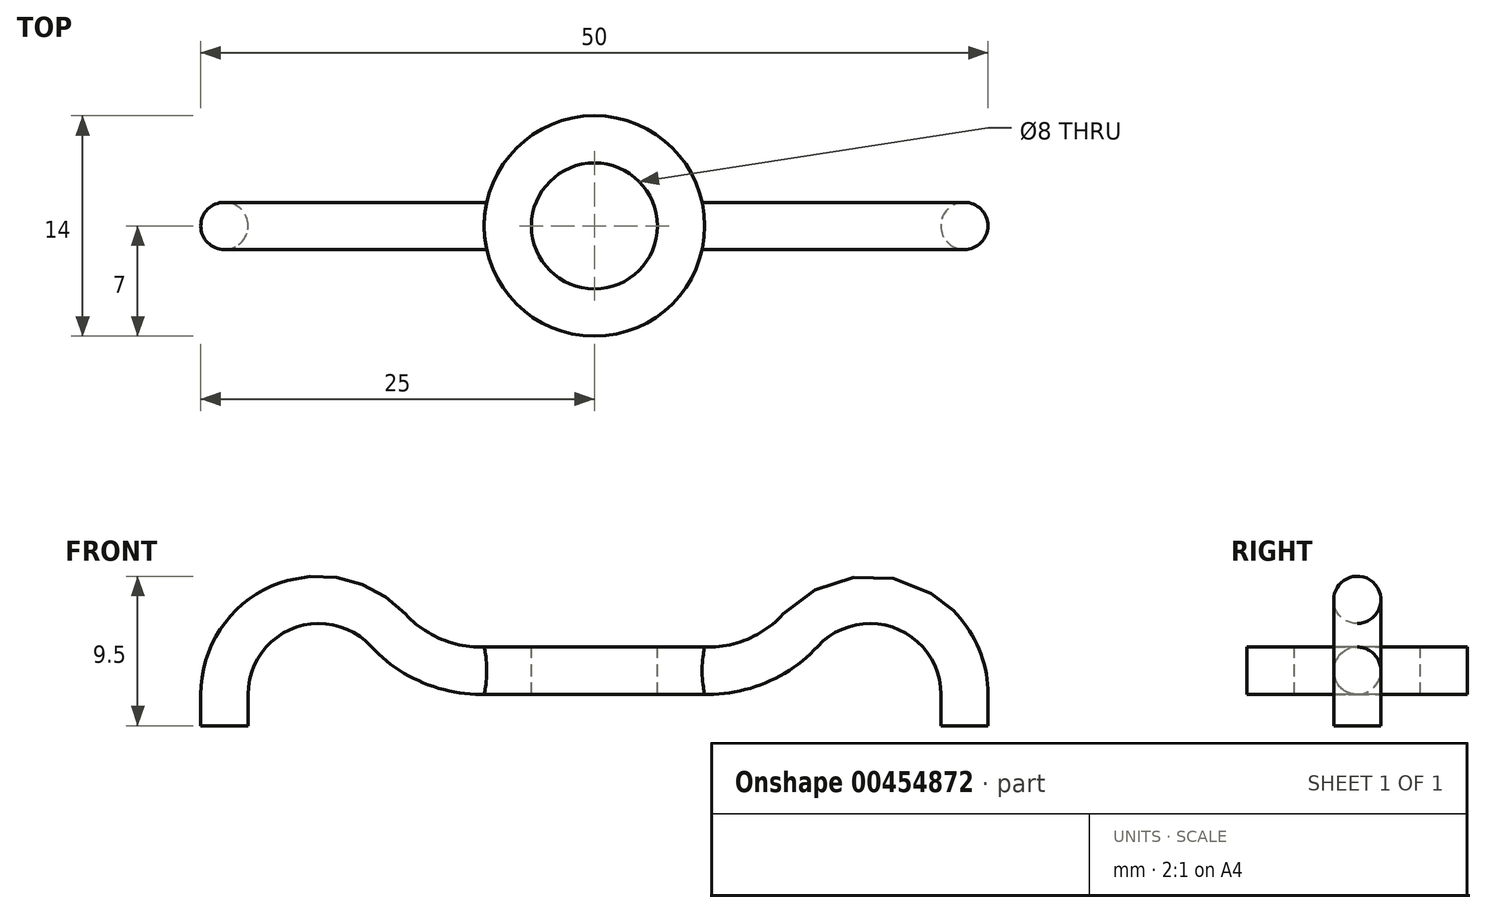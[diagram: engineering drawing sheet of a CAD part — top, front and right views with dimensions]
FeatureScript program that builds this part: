
annotation { "Feature Type Name" : "Feature", "Feature Type Description" : "" }
export const myFeature = defineFeature(function(context is Context, id is Id, definition is map)
    precondition{}
    {
        {
            var Q0;
            Q0=qCreatedBy(makeId("Front.planeOp"),FACE);
            var sketch = newSketch(context, id + "F0", { "sketchPlane" : qUnion([Q0])});
            skLineSegment(sketch, "E0", {"start": v(-25, 0) * mm, "end": v(-25, -2) * mm});
            skLineSegment(sketch, "E1", {"start": v(-7.22, 3) * mm, "end": v(0, 3) * mm});
            skArc(sketch, "E2", {"start": v(-25, 0) * mm, "mid": v(-20.23, 6.98) * mm, "end": v(-12, 5.09) * mm});
            skArc(sketch, "E3", {"start": v(-12, 5.09) * mm, "mid": v(-9.82, 3.55) * mm, "end": v(-7.22, 3) * mm});
            skLineSegment(sketch, "E4.0", {"start": v(-22, 0) * mm, "end": v(-22, -2) * mm});
            skArc(sketch, "E5.0", {"start": v(-22, 0) * mm, "mid": v(-19.14, 4.2) * mm, "end": v(-14.2, 3.05) * mm});
            skArc(sketch, "E6.0", {"start": v(-14.2, 3.05) * mm, "mid": v(-11.02, 0.8) * mm, "end": v(-7.22, 0) * mm});
            skLineSegment(sketch, "E7.0", {"start": v(-7.22, 0) * mm, "end": v(0, 0) * mm});
            skLineSegment(sketch, "E8", {"start": v(-25, -2) * mm, "end": v(-22, -2) * mm});
            skLineSegment(sketch, "E9", {"start": v(0, 3) * mm, "end": v(0, 0) * mm, "construction": true});
            skLineSegment(sketch, "E10.MirrorCS", {"start": v(25, 0) * mm, "end": v(25, -2) * mm});
            skLineSegment(sketch, "E11.MirrorCS", {"start": v(25, -2) * mm, "end": v(22, -2) * mm});
            skArc(sketch, "E12.MirrorCS", {"start": v(25, 0) * mm, "mid": v(20.23, 6.98) * mm, "end": v(12, 5.09) * mm});
            skArc(sketch, "E13.MirrorCS", {"start": v(22, 0) * mm, "mid": v(19.14, 4.2) * mm, "end": v(14.2, 3.05) * mm});
            skArc(sketch, "E14.MirrorCS", {"start": v(12, 5.09) * mm, "mid": v(9.82, 3.55) * mm, "end": v(7.22, 3) * mm});
            skArc(sketch, "E15.MirrorCS", {"start": v(14.2, 3.05) * mm, "mid": v(11.02, 0.8) * mm, "end": v(7.22, 0) * mm});
            skLineSegment(sketch, "E16.MirrorCS", {"start": v(22, 0) * mm, "end": v(22, -2) * mm});
            skLineSegment(sketch, "E17.MirrorCS", {"start": v(7.22, 3) * mm, "end": v(0, 3) * mm});
            skLineSegment(sketch, "E18.MirrorCS", {"start": v(7.22, 0) * mm, "end": v(0, 0) * mm});
            skSolve(sketch);
        }
        {
            var Q0;
            Q0=makeQuery(id+"F0.imprint","IMPRINT",FACE,{"disambiguationData":[TD([[makeQuery(id+"F0.imprint","IMPRINT",EDGE,{"derivedFrom":sQuery(id+"F0.wireOp",EDGE,"E0")}),1.0]])]});
            extrude(context, id + "F1", {"entities" : qUnion([Q0]), "depth" : 3 * mm, "symmetric" : true});
        }
        {
            var Q0;
            Q0=makeQuery(id+"F1.opExtrude","CAP_EDGE",EDGE,{"disambiguationData":[OSD([sQuery(id+"F0.wireOp",EDGE,"E2")])],"isStart":false});
            var Q1;
            Q1=makeQuery(id+"F1.opExtrude","CAP_EDGE",EDGE,{"disambiguationData":[OSD([sQuery(id+"F0.wireOp",EDGE,"E5.0")])],"isStart":false});
            var Q2;
            Q2=makeQuery(id+"F1.opExtrude","CAP_EDGE",EDGE,{"disambiguationData":[OSD([sQuery(id+"F0.wireOp",EDGE,"E2")])],"isStart":true});
            var Q3;
            Q3=makeQuery(id+"F1.opExtrude","CAP_EDGE",EDGE,{"disambiguationData":[OSD([sQuery(id+"F0.wireOp",EDGE,"E5.0")])],"isStart":true});
            fillet(context, id + "F2", {"entities" : qUnion([Q0, Q1, Q2, Q3]), "radius" : 1.5 * mm, "tangentPropagation" : true, "allowEdgeOverflow" : false});
        }
        {
            var Q0;
            Q0=qCreatedBy(makeId("Top.planeOp"),FACE);
            var sketch = newSketch(context, id + "F3", { "sketchPlane" : qUnion([Q0])});
            skCircle(sketch, "E19", {"center": v(0, 0) * mm, "radius": 7 * mm});
            skSolve(sketch);
        }
        {
            var Q0;
            Q0 = qSketchRegion(id + "F3", true);
            extrude(context, id + "F4", {"entities" : qUnion([Q0]), "operationType" : NewBodyOperationType.ADD, "depth" : 3 * mm});
        }
        {
            var Q0;
            Q0=makeQuery(id+"F4.opExtrude","CAP_FACE",FACE,{"disambiguationData":[OSD([sQuery(id+"F3.wireOp",EDGE,"E19")])],"isStart":false});
            var sketch = newSketch(context, id + "F5", { "sketchPlane" : qUnion([Q0])});
            skCircle(sketch, "E20", {"center": v(0, 0) * mm, "radius": 4 * mm});
            skSolve(sketch);
        }
        {
            var Q0;
            Q0=makeQuery(id+"F5.imprint","IMPRINT",FACE,{"disambiguationData":[TD([[makeQuery(id+"F5.imprint","IMPRINT",EDGE,{"derivedFrom":sQuery(id+"F5.wireOp",EDGE,"E20")}),1.0]])]});
            extrude(context, id + "F6", {"entities" : qUnion([Q0]), "operationType" : NewBodyOperationType.REMOVE, "oppositeDirection" : true, "depth" : 25 * mm});
        }
    });
